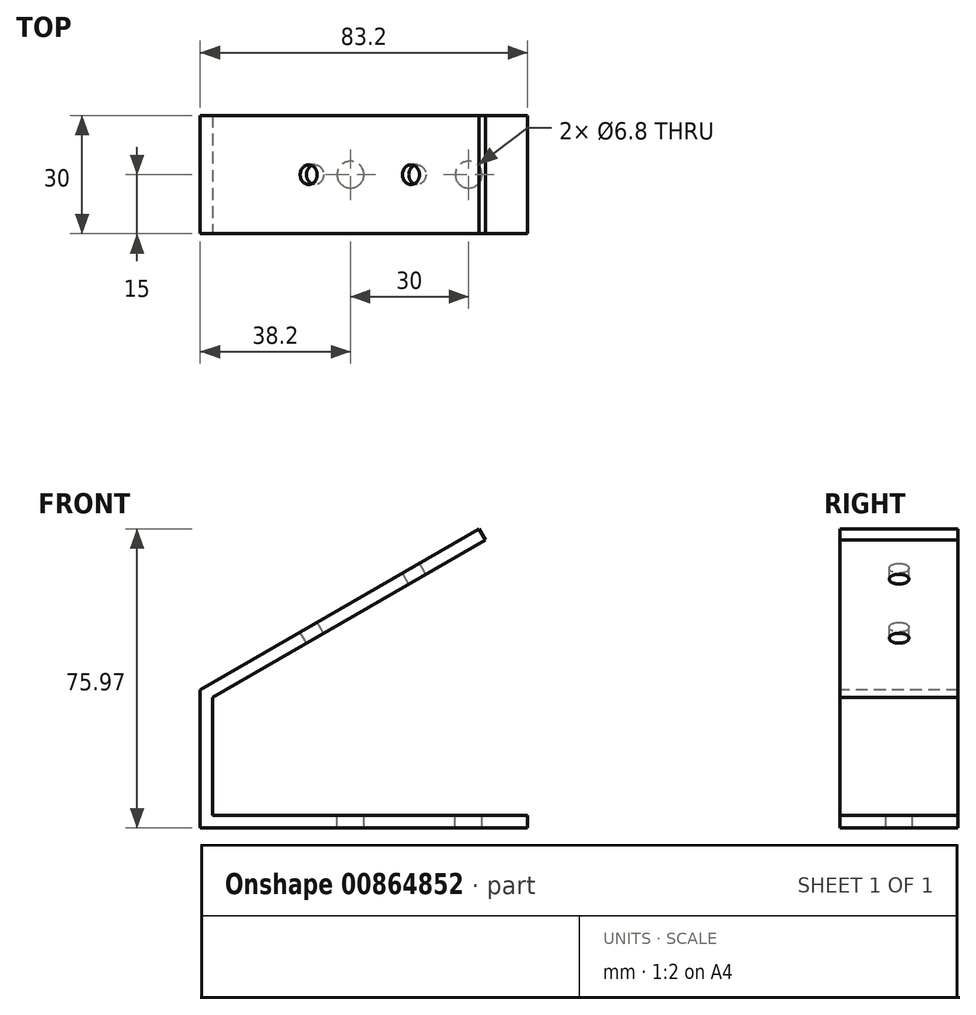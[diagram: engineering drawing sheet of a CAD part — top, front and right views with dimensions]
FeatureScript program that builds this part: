
annotation { "Feature Type Name" : "Feature", "Feature Type Description" : "" }
export const myFeature = defineFeature(function(context is Context, id is Id, definition is map)
    precondition{}
    {
        {
            var Q0;
            Q0=qCreatedBy(makeId("Front.planeOp"),FACE);
            var sketch = newSketch(context, id + "F0", { "sketchPlane" : qUnion([Q0])});
            skLineSegment(sketch, "E0", {"start": v(0, 0) * mm, "end": v(80, 0) * mm});
            skLineSegment(sketch, "E1", {"start": v(0, 0) * mm, "end": v(0, 30) * mm});
            skLineSegment(sketch, "E2", {"start": v(0, 30) * mm, "end": v(69.28, 70) * mm});
            skLineSegment(sketch, "E3.0", {"start": v(-3.2, 31.85) * mm, "end": v(67.68, 72.77) * mm});
            skLineSegment(sketch, "E3.1", {"start": v(-3.2, -3.2) * mm, "end": v(-3.2, 31.85) * mm});
            skLineSegment(sketch, "E3.2", {"start": v(-3.2, -3.2) * mm, "end": v(80, -3.2) * mm});
            skLineSegment(sketch, "E4", {"start": v(67.68, 72.77) * mm, "end": v(69.28, 70) * mm});
            skLineSegment(sketch, "E5", {"start": v(80, 0) * mm, "end": v(80, -3.2) * mm});
            skSolve(sketch);
        }
        {
            var Q0;
            Q0 = qSketchRegion(id + "F0", true);
            extrude(context, id + "F1", {"entities" : qUnion([Q0]), "oppositeDirection" : true, "depth" : 30 * mm, "offsetDistance" : 25 * mm});
        }
        {
            var Q0;
            Q0=qCreatedBy(makeId("Top.planeOp"),FACE);
            var sketch = newSketch(context, id + "F2", { "sketchPlane" : qUnion([Q0])});
            skPoint(sketch, "E6", {"position": v(65, 15) * mm});
            skPoint(sketch, "E7", {"position": v(35, 15) * mm});
            skSolve(sketch);
        }
        {
            var Q0;
            Q0=sQuery(id+"F2.wireOp",VERTEX,"E7");
            var Q1;
            Q1=sQuery(id+"F2.wireOp",VERTEX,"E6");
            var Q2;
            Q2=makeQuery(id+"F1.opExtrude","SWEPT_BODY",BODY,{"disambiguationData":[OSD([sQuery(id+"F0.wireOp",EDGE,"E0"),sQuery(id+"F0.wireOp",EDGE,"E1"),sQuery(id+"F0.wireOp",EDGE,"E2"),sQuery(id+"F0.wireOp",EDGE,"E3.0"),sQuery(id+"F0.wireOp",EDGE,"E3.1"),sQuery(id+"F0.wireOp",EDGE,"E3.2"),sQuery(id+"F0.wireOp",EDGE,"E4"),sQuery(id+"F0.wireOp",EDGE,"E5")])]});
            hole(context, id + "F3", {"style" : HoleStyle.SIMPLE, "endStyle" : HoleEndStyle.THROUGH, "standardTappedOrClearance" : lookupTablePath({ "standard" : "ISO", "engagement" : "75%", "pitch" : "1.25 mm", "size" : "M8", "type" : "Tapped" }), "standardBlindInLast" : lookupTablePath({ "standard" : "ISO", "engagement" : "75%", "pitch" : "1.25 mm", "size" : "M8", "type" : "Tapped" }), "holeDiameter" : 6.8 * mm, "majorDiameter" : 8 * mm, "showTappedDepth" : true, "tappedDepth" : 3.2 * mm, "tapClearance" : 3, "locations" : qUnion([Q0, Q1]), "scope" : qUnion([Q2])});
        }
        {
            var Q0;
            Q0=makeQuery(id+"F1.opExtrude","SWEPT_FACE",FACE,{"disambiguationData":[OSD([sQuery(id+"F0.wireOp",EDGE,"E3.0")])]});
            var sketch = newSketch(context, id + "F4", { "sketchPlane" : qUnion([Q0])});
            skPoint(sketch, "E8", {"position": v(75, 15) * mm});
            skPoint(sketch, "E9", {"position": v(45, 15) * mm});
            skSolve(sketch);
        }
        {
            var Q0;
            Q0=sQuery(id+"F4.wireOp",VERTEX,"E8");
            var Q1;
            Q1=sQuery(id+"F4.wireOp",VERTEX,"E9");
            var Q2;
            Q2=makeQuery(id+"F1.opExtrude","SWEPT_BODY",BODY,{"disambiguationData":[OSD([sQuery(id+"F0.wireOp",EDGE,"E0"),sQuery(id+"F0.wireOp",EDGE,"E1"),sQuery(id+"F0.wireOp",EDGE,"E2"),sQuery(id+"F0.wireOp",EDGE,"E3.0"),sQuery(id+"F0.wireOp",EDGE,"E3.1"),sQuery(id+"F0.wireOp",EDGE,"E3.2"),sQuery(id+"F0.wireOp",EDGE,"E4"),sQuery(id+"F0.wireOp",EDGE,"E5")])]});
            hole(context, id + "F5", {"style" : HoleStyle.SIMPLE, "endStyle" : HoleEndStyle.BLIND, "standardTappedOrClearance" : lookupTablePath({ "standard" : "ISO", "engagement" : "75%", "pitch" : "1 mm", "size" : "M6", "type" : "Tapped" }), "standardBlindInLast" : lookupTablePath({ "standard" : "ISO", "engagement" : "75%", "pitch" : "1 mm", "size" : "M6", "type" : "Tapped" }), "holeDiameter" : 5 * mm, "majorDiameter" : 6 * mm, "showTappedDepth" : true, "holeDepth" : 6.2 * mm, "tappedDepth" : 3.2 * mm, "tapClearance" : 3, "locations" : qUnion([Q0, Q1]), "scope" : qUnion([Q2])});
        }
    });
